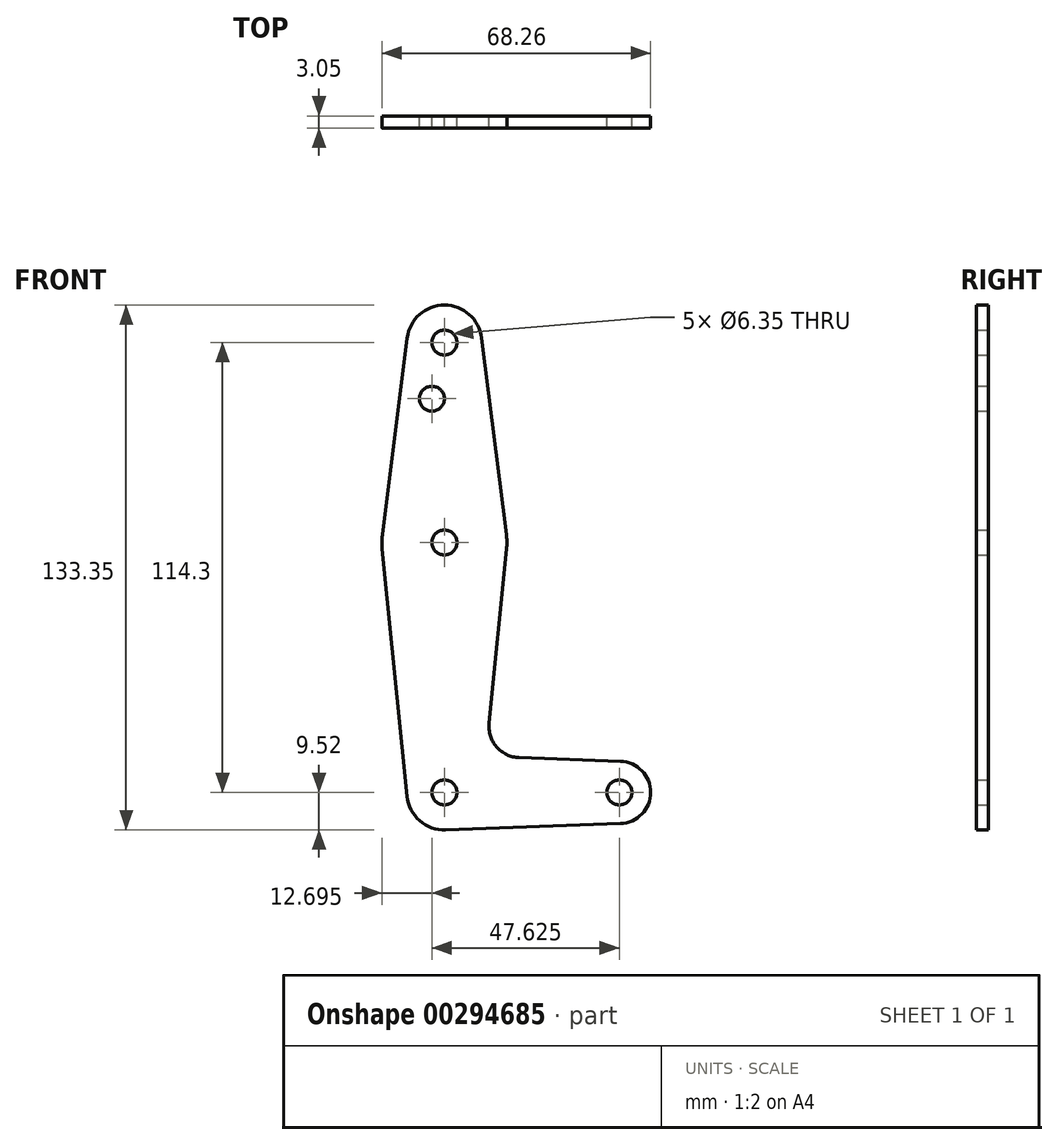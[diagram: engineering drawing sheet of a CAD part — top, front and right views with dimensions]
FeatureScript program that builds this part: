
annotation { "Feature Type Name" : "Feature", "Feature Type Description" : "" }
export const myFeature = defineFeature(function(context is Context, id is Id, definition is map)
    precondition{}
    {
        {
            var Q0;
            Q0=qCreatedBy(makeId("Front.planeOp"),FACE);
            var sketch = newSketch(context, id + "F0", { "sketchPlane" : qUnion([Q0])});
            skCircle(sketch, "E0", {"center": v(0, 0) * mm, "radius": 9.52 * mm});
            skCircle(sketch, "E1", {"center": v(44.45, 0) * mm, "radius": 7.94 * mm});
            skCircle(sketch, "E2", {"center": v(0, 63.5) * mm, "radius": 15.88 * mm});
            skCircle(sketch, "E3", {"center": v(0, 114.3) * mm, "radius": 9.53 * mm});
            skLineSegment(sketch, "E4", {"start": v(0, 114.3) * mm, "end": v(0, 63.5) * mm, "construction": true});
            skLineSegment(sketch, "E5", {"start": v(0, 63.5) * mm, "end": v(0, 0) * mm, "construction": true});
            skLineSegment(sketch, "E6", {"start": v(0, 0) * mm, "end": v(44.45, 0) * mm, "construction": true});
            skLineSegment(sketch, "E7", {"start": v(-9.45, 115.5) * mm, "end": v(-15.75, 65.48) * mm});
            skLineSegment(sketch, "E8", {"start": v(9.45, 115.5) * mm, "end": v(15.75, 65.48) * mm});
            skLineSegment(sketch, "E9", {"start": v(-15.8, 61.91) * mm, "end": v(-9.48, -0.95) * mm});
            skLineSegment(sketch, "E10", {"start": v(15.8, 61.91) * mm, "end": v(11.34, 17.6) * mm});
            skLineSegment(sketch, "E11", {"start": v(18.97, 8.85) * mm, "end": v(44.73, 7.93) * mm});
            skLineSegment(sketch, "E12", {"start": v(44.73, -7.93) * mm, "end": v(0.34, -9.52) * mm});
            skCircle(sketch, "E13", {"center": v(0, 114.3) * mm, "radius": 3.18 * mm});
            skCircle(sketch, "E14", {"center": v(0, 63.5) * mm, "radius": 3.17 * mm});
            skCircle(sketch, "E15", {"center": v(0, 0) * mm, "radius": 3.17 * mm});
            skCircle(sketch, "E16", {"center": v(44.45, 0) * mm, "radius": 3.18 * mm});
            skCircle(sketch, "E17", {"center": v(-3.18, 100.03) * mm, "radius": 3.18 * mm});
            skArc(sketch, "E18.filletArc", {"start": v(11.34, 17.6) * mm, "mid": v(13.26, 11.57) * mm, "end": v(18.97, 8.85) * mm});
            skSolve(sketch);
        }
        {
            var Q0;
            Q0 = qSketchRegion(id + "F0", true);
            extrude(context, id + "F1", {"entities" : qUnion([Q0]), "depth" : 3.05 * mm});
        }
    });
